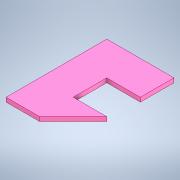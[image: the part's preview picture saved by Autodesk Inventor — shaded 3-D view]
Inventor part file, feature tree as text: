
AUTODESK INVENTOR PART (.ipt)
format: ipt  version: 2020 (Build 240168000, 168)  size: 98,304 bytes
history: native  units: in
note: dims shown in document units (in); Inventor stores cm internally (conversion verified against a paired STEP export)
features: extrude x1, sketch x1
ambient origin geometry x8: Origin, YZ Plane, XZ Plane, XY Plane, X Axis, Y Axis, Z Axis, Center Point
bodies: Solid1 (feature_tree)
feature tree (2):
  extrude  "Extrusion1"  Depth=1.0in
  sketch  "Sketch1"  dims[d0=0.5in d1=1.0in d2=0.5in d4=0.063in d5=0.0in]
